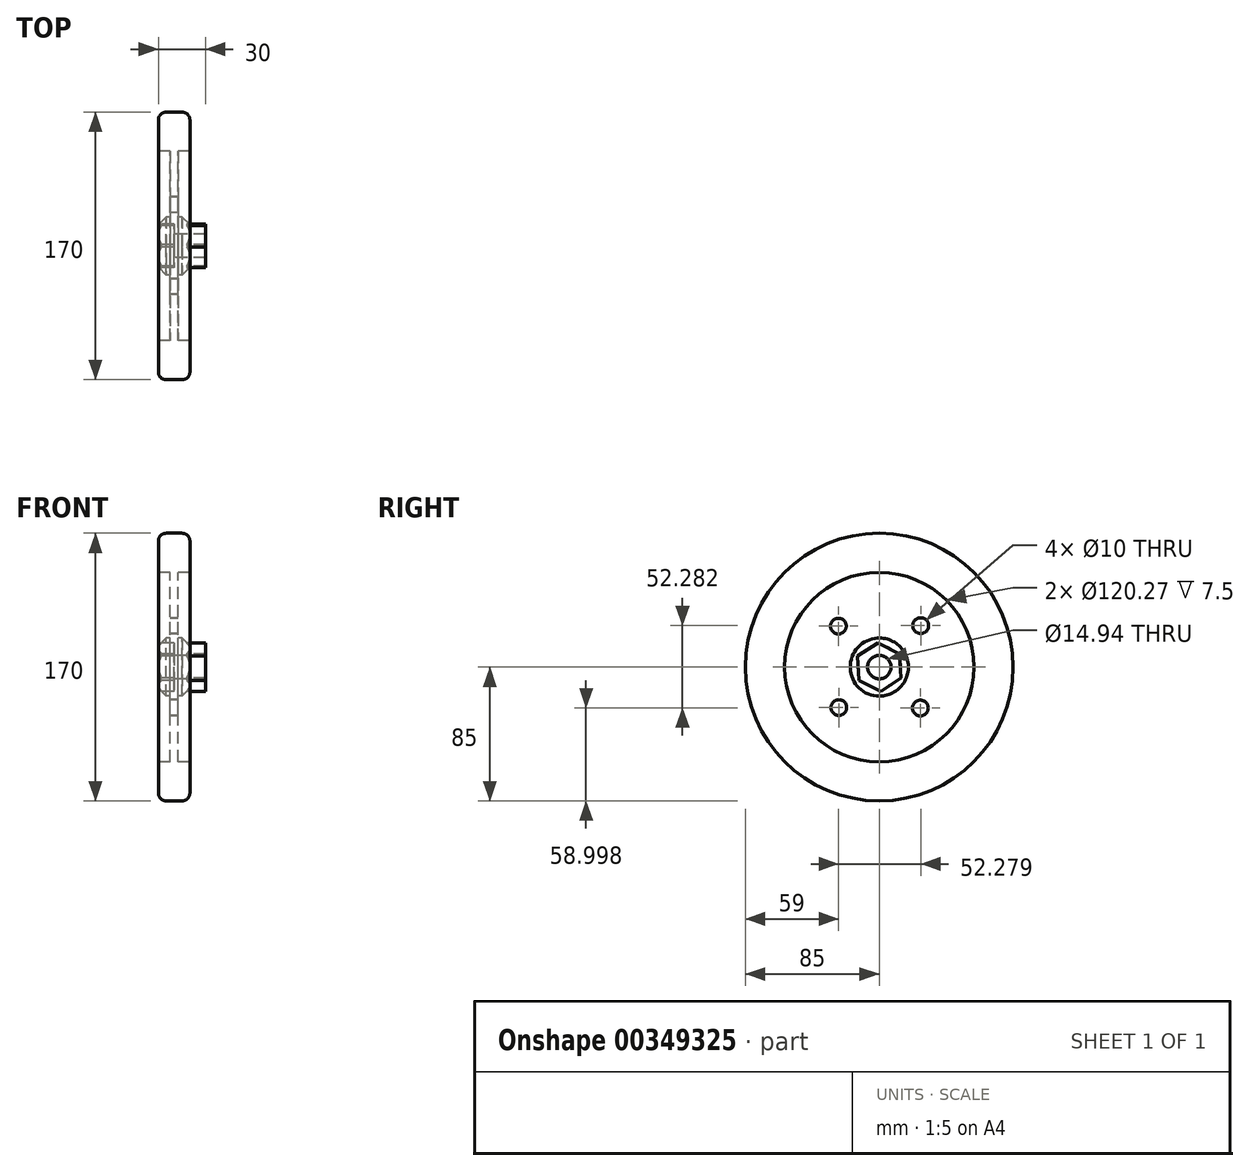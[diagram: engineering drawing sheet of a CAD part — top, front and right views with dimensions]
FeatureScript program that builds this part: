
annotation { "Feature Type Name" : "Feature", "Feature Type Description" : "" }
export const myFeature = defineFeature(function(context is Context, id is Id, definition is map)
    precondition{}
    {
        {
            var Q0;
            Q0=qCreatedBy(makeId("Right.planeOp"),FACE);
            var sketch = newSketch(context, id + "F0", { "sketchPlane" : qUnion([Q0])});
            skCircle(sketch, "E0", {"center": v(0, 0) * mm, "radius": 85 * mm});
            skCircle(sketch, "E1", {"center": v(0, 0) * mm, "radius": 60.13 * mm});
            skCircle(sketch, "E2", {"center": v(0, 0) * mm, "radius": 18.46 * mm});
            skCircle(sketch, "E3", {"center": v(0, 0) * mm, "radius": 7.47 * mm});
            skCircle(sketch, "E4", {"center": v(26.28, 26.28) * mm, "radius": 5 * mm});
            skCircle(sketch, "E5", {"center": v(-26, 26) * mm, "radius": 5 * mm});
            skCircle(sketch, "E6", {"center": v(-25.73, -25.73) * mm, "radius": 5 * mm});
            skCircle(sketch, "E7", {"center": v(26.04, -26) * mm, "radius": 5 * mm});
            skCircle(sketch, "E8.cCircle", {"center": v(0, 0) * mm, "radius": 13.35 * mm, "construction": true});
            skLineSegment(sketch, "E8.0", {"start": v(13.77, -6.95) * mm, "end": v(0.87, -15.4) * mm});
            skLineSegment(sketch, "E8.1", {"start": v(0.87, -15.4) * mm, "end": v(-12.9, -8.45) * mm});
            skLineSegment(sketch, "E8.2", {"start": v(-12.9, -8.45) * mm, "end": v(-13.77, 6.95) * mm});
            skLineSegment(sketch, "E8.3", {"start": v(-13.77, 6.95) * mm, "end": v(-0.87, 15.4) * mm});
            skLineSegment(sketch, "E8.4", {"start": v(-0.87, 15.4) * mm, "end": v(12.9, 8.45) * mm});
            skLineSegment(sketch, "E8.5", {"start": v(12.9, 8.45) * mm, "end": v(13.77, -6.95) * mm});
            skPoint(sketch, "E8.0.midPoint", {"position": v(7.32, -11.17) * mm});
            skSolve(sketch);
        }
        {
            var Q0;
            Q0=makeQuery(id+"F0.imprint","IMPRINT",FACE,{"disambiguationData":[TD([[makeQuery(id+"F0.imprint","IMPRINT",EDGE,{"derivedFrom":sQuery(id+"F0.wireOp",EDGE,"E0")}),1.0]])]});
            extrude(context, id + "F1", {"entities" : qUnion([Q0]), "endBound" : BoundingType.SYMMETRIC, "depth" : 20 * mm});
        }
        {
            var Q0;
            Q0=makeQuery(id+"F0.imprint","IMPRINT",FACE,{"disambiguationData":[TD([[makeQuery(id+"F0.imprint","IMPRINT",EDGE,{"derivedFrom":sQuery(id+"F0.wireOp",EDGE,"E1")}),1.0]])]});
            extrude(context, id + "F2", {"entities" : qUnion([Q0]), "operationType" : NewBodyOperationType.ADD, "endBound" : BoundingType.SYMMETRIC, "depth" : 5 * mm});
        }
        {
            var Q0;
            Q0=makeQuery(id+"F0.imprint","IMPRINT",FACE,{"disambiguationData":[TD([[makeQuery(id+"F0.imprint","IMPRINT",EDGE,{"derivedFrom":sQuery(id+"F0.wireOp",EDGE,"E2")}),1.0]])]});
            extrude(context, id + "F3", {"entities" : qUnion([Q0]), "operationType" : NewBodyOperationType.ADD, "endBound" : BoundingType.SYMMETRIC, "depth" : 20 * mm});
        }
        {
            var Q0;
            Q0=makeQuery(id+"F1.opExtrude","CAP_EDGE",EDGE,{"disambiguationData":[OSD([sQuery(id+"F0.wireOp",EDGE,"E0")])],"isStart":true});
            var Q1;
            Q1=makeQuery(id+"F1.opExtrude","CAP_EDGE",EDGE,{"disambiguationData":[OSD([sQuery(id+"F0.wireOp",EDGE,"E0")])],"isStart":false});
            fillet(context, id + "F4", {"entities" : qUnion([Q0, Q1]), "radius" : 5 * mm, "tangentPropagation" : true, "allowEdgeOverflow" : false});
        }
        {
            var Q0;
            Q0=makeQuery(id+"F3.opExtrude","CAP_EDGE",EDGE,{"disambiguationData":[OSD([sQuery(id+"F0.wireOp",EDGE,"E2")])],"isStart":false});
            var Q1;
            Q1=makeQuery(id+"F3.opExtrude","CAP_EDGE",EDGE,{"disambiguationData":[OSD([sQuery(id+"F0.wireOp",EDGE,"E2")])],"isStart":true});
            chamfer(context, id + "F5", {"entities" : qUnion([Q0, Q1]), "width" : 5 * mm, "tangentPropagation" : true});
        }
        {
            var Q0;
            Q0=makeQuery(id+"F0.imprint","IMPRINT",FACE,{"disambiguationData":[TD([[makeQuery(id+"F0.imprint","IMPRINT",EDGE,{"derivedFrom":sQuery(id+"F0.wireOp",EDGE,"E3")}),-1.0]])]});
            extrude(context, id + "F6", {"entities" : qUnion([Q0]), "operationType" : NewBodyOperationType.ADD, "depth" : 20 * mm});
        }
    });
